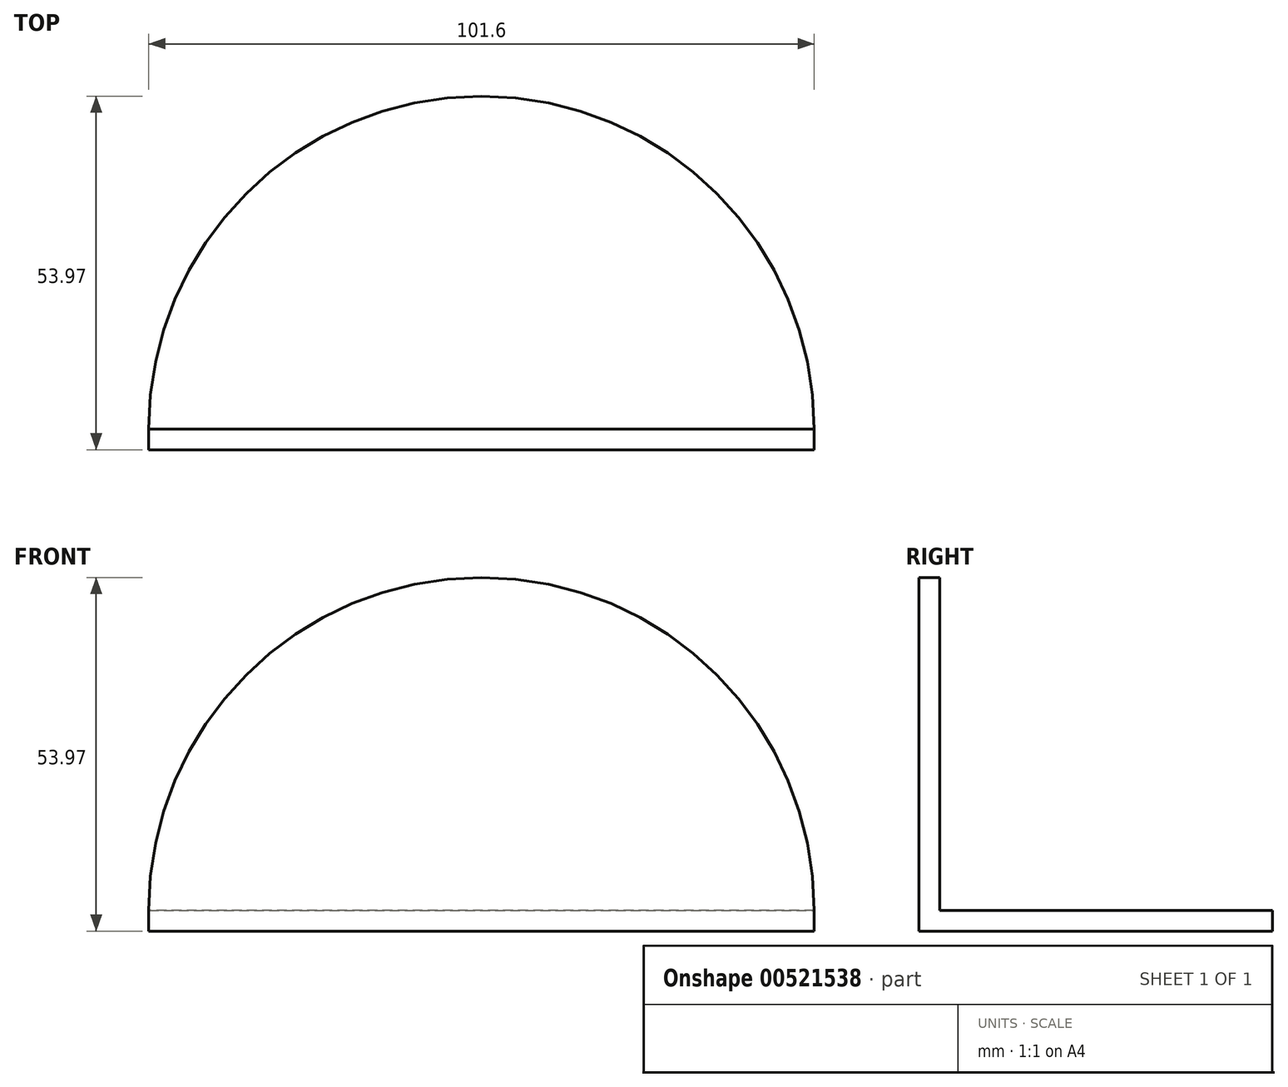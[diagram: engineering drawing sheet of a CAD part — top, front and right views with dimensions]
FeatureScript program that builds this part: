
annotation { "Feature Type Name" : "Feature", "Feature Type Description" : "" }
export const myFeature = defineFeature(function(context is Context, id is Id, definition is map)
    precondition{}
    {
        {
            var Q0;
            Q0=qCreatedBy(makeId("Top.planeOp"),FACE);
            var sketch = newSketch(context, id + "F0", { "sketchPlane" : qUnion([Q0])});
            skArc(sketch, "E0", {"start": v(50.8, 0) * mm, "mid": v(0, 50.8) * mm, "end": v(-50.8, 0) * mm});
            skLineSegment(sketch, "E1", {"start": v(-50.8, 0) * mm, "end": v(50.8, 0) * mm});
            skSolve(sketch);
        }
        {
            var Q0;
            Q0=makeQuery(id+"F0.imprint","IMPRINT",FACE,{"disambiguationData":[TD([[makeQuery(id+"F0.imprint","IMPRINT",EDGE,{"derivedFrom":sQuery(id+"F0.wireOp",EDGE,"E0")}),1.0]])]});
            extrude(context, id + "F1", {"entities" : qUnion([Q0]), "depth" : 3.17 * mm, "offsetDistance" : 25.4 * mm});
        }
        {
            var Q0;
            Q0=makeQuery(id+"F1.opExtrude","SWEPT_FACE",FACE,{"disambiguationData":[OSD([sQuery(id+"F0.wireOp",EDGE,"E1")])]});
            var sketch = newSketch(context, id + "F2", { "sketchPlane" : qUnion([Q0])});
            skArc(sketch, "E2", {"start": v(-50.8, 3.18) * mm, "mid": v(0, 53.98) * mm, "end": v(50.8, 3.18) * mm});
            skLineSegment(sketch, "E3", {"start": v(-50.8, 3.18) * mm, "end": v(50.8, 3.18) * mm});
            skSolve(sketch);
        }
        {
            var Q0;
            Q0 = qSketchRegion(id + "F2", true);
            extrude(context, id + "F3", {"entities" : qUnion([Q0]), "operationType" : NewBodyOperationType.ADD, "depth" : 3.17 * mm, "offsetDistance" : 25.4 * mm});
        }
        {
            var Q0;
            Q0=qCreatedBy(makeId("Right.planeOp"),FACE);
            var sketch = newSketch(context, id + "F4", { "sketchPlane" : qUnion([Q0])});
            skLineSegment(sketch, "E4.bottom", {"start": v(0, 0) * mm, "end": v(-3.17, 0) * mm});
            skLineSegment(sketch, "E4.top", {"start": v(0, 3.18) * mm, "end": v(-3.18, 3.18) * mm});
            skLineSegment(sketch, "E4.left", {"start": v(0, 3.18) * mm, "end": v(0, 0) * mm});
            skLineSegment(sketch, "E4.right", {"start": v(-3.18, 3.18) * mm, "end": v(-3.17, 0) * mm});
            skSolve(sketch);
        }
        {
            var Q0;
            Q0 = qSketchRegion(id + "F4", true);
            var Q1;
            {var subQ0=sQuery(id+"F0.wireOp",EDGE,"E1");var subQ1=sQuery(id+"F0.wireOp",EDGE,"E0");Q1=makeQuery(id+"F1.opExtrude","CAP_VERTEX",VERTEX,{"disambiguationData":[OSD([subQ1,subQ0]),TDD([makeQuery(id+"F0.imprint","INTERSECT",VERTEX,{"disambiguationData":[OD(0.0)],"derivedFrom":[subQ1,subQ0]})])],"isStart":true});}
            var Q2;
            {var subQ0=sQuery(id+"F0.wireOp",EDGE,"E1");var subQ1=sQuery(id+"F0.wireOp",EDGE,"E0");Q2=makeQuery(id+"F1.opExtrude","CAP_VERTEX",VERTEX,{"disambiguationData":[OSD([subQ1,subQ0]),TDD([makeQuery(id+"F0.imprint","INTERSECT",VERTEX,{"disambiguationData":[OD(1.0)],"derivedFrom":[subQ1,subQ0]})])],"isStart":true});}
            extrude(context, id + "F5", {"entities" : qUnion([Q0]), "operationType" : NewBodyOperationType.ADD, "endBound" : BoundingType.UP_TO_VERTEX, "depth" : 25.4 * mm, "endBoundEntityVertex" : qUnion([Q1]), "offsetDistance" : 25.4 * mm, "hasSecondDirection" : true, "secondDirectionBound" : SecondDirectionBoundingType.UP_TO_VERTEX, "secondDirectionOppositeDirection" : true, "secondDirectionDepth" : 25.4 * mm, "secondDirectionBoundEntityVertex" : qUnion([Q2])});
        }
    });
